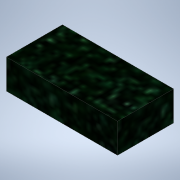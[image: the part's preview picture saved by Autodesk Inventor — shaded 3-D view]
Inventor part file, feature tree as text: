
AUTODESK INVENTOR PART (.ipt)
format: ipt  version: 2020.2 (Build 242310000, 310)  size: 128,512 bytes
history: native  units: mm
features: other x2, sketch x2, extrude x1
ambient origin geometry x8: Origin, YZ Plane, XZ Plane, XY Plane, X Axis, Y Axis, Z Axis, Center Point
bodies: Body1 (feature_tree)
feature tree (5):
  other  "ソリッド1"
  extrude  "押し出し1"  Depth=93.0mm
  sketch  "スケッチ3"
  sketch  "スケッチ1"
  other  "断面エッジを投影2"
